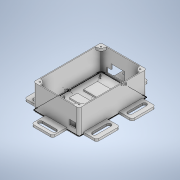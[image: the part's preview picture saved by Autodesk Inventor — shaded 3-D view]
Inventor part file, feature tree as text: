
AUTODESK INVENTOR PART (.ipt)
format: ipt  version: 2021 (Build 250183000, 183)  size: 581,120 bytes
history: native  units: in
note: dims shown in document units (in); Inventor stores cm internally (conversion verified against a paired STEP export)
features: sketch x27, extrude x21, reference x13, plane x7, mirror x7, other x4, fillet x3, revolve x2, chamfer x1
ambient origin geometry x8: Origin, YZ Plane, XZ Plane, XY Plane, X Axis, Y Axis, Z Axis, Center Point
bodies: Solid1 (feature_tree)
feature tree (85):
  sketch  "Sketch1"  dims[d0=3.937in d1=5.9055in]
  extrude  "Extrusion1"  Depth=5.9055in
  extrude  "Extrusion2"  Depth=2.1654in TaperAngle=0.0deg
  sketch  "Sketch2"  dims[d5=0.0787in d6=0.0in d7=-1.5748in]
  plane  "Work Plane1"
  extrude  "Extrusion3"  [1 undecoded]
  sketch  "Sketch7"  dims[d19=0.1181in d20=0.0in d21=2.8346in]
  plane  "Work Plane2"
  revolve  "Revolution2"  [1 undecoded]
  plane  "Work Plane3"
  extrude  "Extrusion4"  Depth=1.0236in
  sketch  "Sketch Driven Pattern1"  dims[d2=0.0787in d3=2.1654in d4=0.0in]
  plane  "Work Plane4"
  extrude  "Extrusion21"  Depth=2.8346in
  extrude  "Extrusion6"  Depth=0.1102in
  extrude  "Extrusion7"  Depth=0.1457in
  extrude  "Extrusion8"  TaperAngle=90.0deg  [1 undecoded]
  mirror  "Mirror1"
  plane  "Work Plane5"
  extrude  "Extrusion9"  Depth=0.0157in
  extrude  "Extrusion10"  Depth=0.0299in
  extrude  "Extrusion11"  Depth=1.1811in
  chamfer  "Chamfer1"  Distance=0.5933in
  extrude  "Extrusion12"  Depth=0.4409in
  sketch  "Sketch22"  dims[d46=0.3819in d47=0.5933in d48=0.0in]
  plane  "Work Plane6"
  revolve  "Revolution3"  [1 undecoded]
  extrude  "Extrusion13"  Depth=0.5933in TaperAngle=0.0deg
  sketch  "Sketch Driven Pattern2"  dims[d15=1.378in d16=1.2598in]
  extrude  "Extrusion14"  Depth=0.3937in
  extrude  "Extrusion15"  Depth=0.4606in
  extrude  "Extrusion16"  Depth=0.5933in TaperAngle=0.0deg
  plane  "Work Plane7"
  mirror  "Mirror2"
  extrude  "Extrusion17"  Depth=0.4409in
  extrude  "Extrusion18"  Depth=0.5933in TaperAngle=0.0deg
  extrude  "Extrusion19"  Depth=0.5933in TaperAngle=0.0deg
  mirror  "Mirror3"
  mirror  "Mirror4"
  fillet  "Fillet1"  Radius=0.2756in
  extrude  "Extrusion20"  Depth=0.5906in TaperAngle=0.0deg
  fillet  "Fillet2"  [1 undecoded]
  mirror  "Mirror5"
  extrude  "Extrusion22"  Depth=0.1969in TaperAngle=0.0deg
  fillet  "Fillet3"  Radius=0.2362in
  mirror  "Mirror6"
  mirror  "Mirror7"
  sketch  "Sketch6"  dims[d17=1.0236in d18=0.7087in]
  reference  "Reference1"
  reference  "Reference2"
  reference  "Reference3"
  reference  "Reference4"
  sketch  "Sketch8"  dims[d22=0.7087in d23=0.1102in]
  sketch  "Sketch9"  dims[d26=0.1063in d27=0.1457in]
  sketch  "Sketch11"  dims[d28=0.1929in d30=90.0deg]
  sketch  "Sketch13"  dims[d31=3.0in d32=0.0157in]
  sketch  "Sketch15"  dims[d33=0.1946in d34=0.0299in]
  sketch  "Sketch18"  dims[d35=0.0787in d36=0.0in d42=1.1811in]
  sketch  "Sketch19"  dims[d43=0.4606in]
  sketch  "Sketch20"  dims[d44=0.9843in]
  sketch  "Sketch21"  dims[d45=0.0906in]
  reference  "Reference11"
  reference  "Reference12"
  reference  "Reference13"
  reference  "Reference14"
  reference  "Reference15"
  reference  "Reference16"
  sketch  "Sketch25"  dims[d49=0.0866in d50=0.4409in]
  sketch  "Sketch26"  dims[d51=0.3236in d52=0.5933in d53=0.0in]
  sketch  "Sketch27"  dims[d54=0.4724in d55=0.5933in d56=0.0in]
  sketch  "Sketch29"  dims[d57=0.1575in d58=0.0787in d59=45.0deg d63=0.3937in]
  sketch  "Sketch30"  dims[d64=0.0906in d65=0.4606in]
  sketch  "Sketch31"  dims[d66=0.9843in d67=0.5933in d68=0.0in]
  sketch  "Sketch34"  dims[d69=0.0866in d70=0.4409in]
  sketch  "Sketch35"  dims[d71=0.3236in d72=0.5933in d73=0.0in]
  sketch  "Sketch36"  dims[d74=0.4724in d75=0.5933in d76=0.0in d77=0.2756in]
  sketch  "Sketch37"  dims[d78=0.5906in d79=0.1181in d80=0.0in d81=90.0deg]
  reference  "Reference17"
  sketch  "Sketch38"  dims[d82=0.0157in d83=0.0394in d84=0.0in d85=0.2362in d86=0.5906in d87=0.3937in d88=0.2697in d89=0.0in d90=0.1496in d91=0.0591in d92=0.0in d93=0.0906in d94=0.1969in d95=0.0in d96=0.689in d98=0.4724in d99=0.2362in d100=0.0in d101=0.2362in d102=0.2165in d103=0.2165in d104=0.0984in d105=0.0in d106=0.1299in d107=0.0in d108=0.0in d109=0.1969in d110=0.1969in d111=0.0in d112=0.0157in d113=0.0157in d114=0.9055in d115=0.9055in d116=0.0in d117=1.8898in d118=1.2598in d120=1.6535in d121=0.3937in d122=0.1969in d123=0.5906in d124=1.6929in d125=0.1969in d126=2.0866in d127=0.3937in d128=1.1811in d129=0.3937in d130=0.3937in d131=0.1969in d132=0.0in d133=0.1969in d134=0.0039in d135=0.0079in]
  reference  "Reference18"
  reference  "Reference19"
  other  "Chestbox_with_electronical_devices.iam"
  other  "ArduinoMega_STEP_AP203:1"
  other  "TCA9548A Adfruit with Header:1"
  other  "Part57"
note: 5 required parameter values undecoded (feature->parameter linkage not recoverable at this tier; creation-order binding heuristic only, values carry confidence <= 0.55)